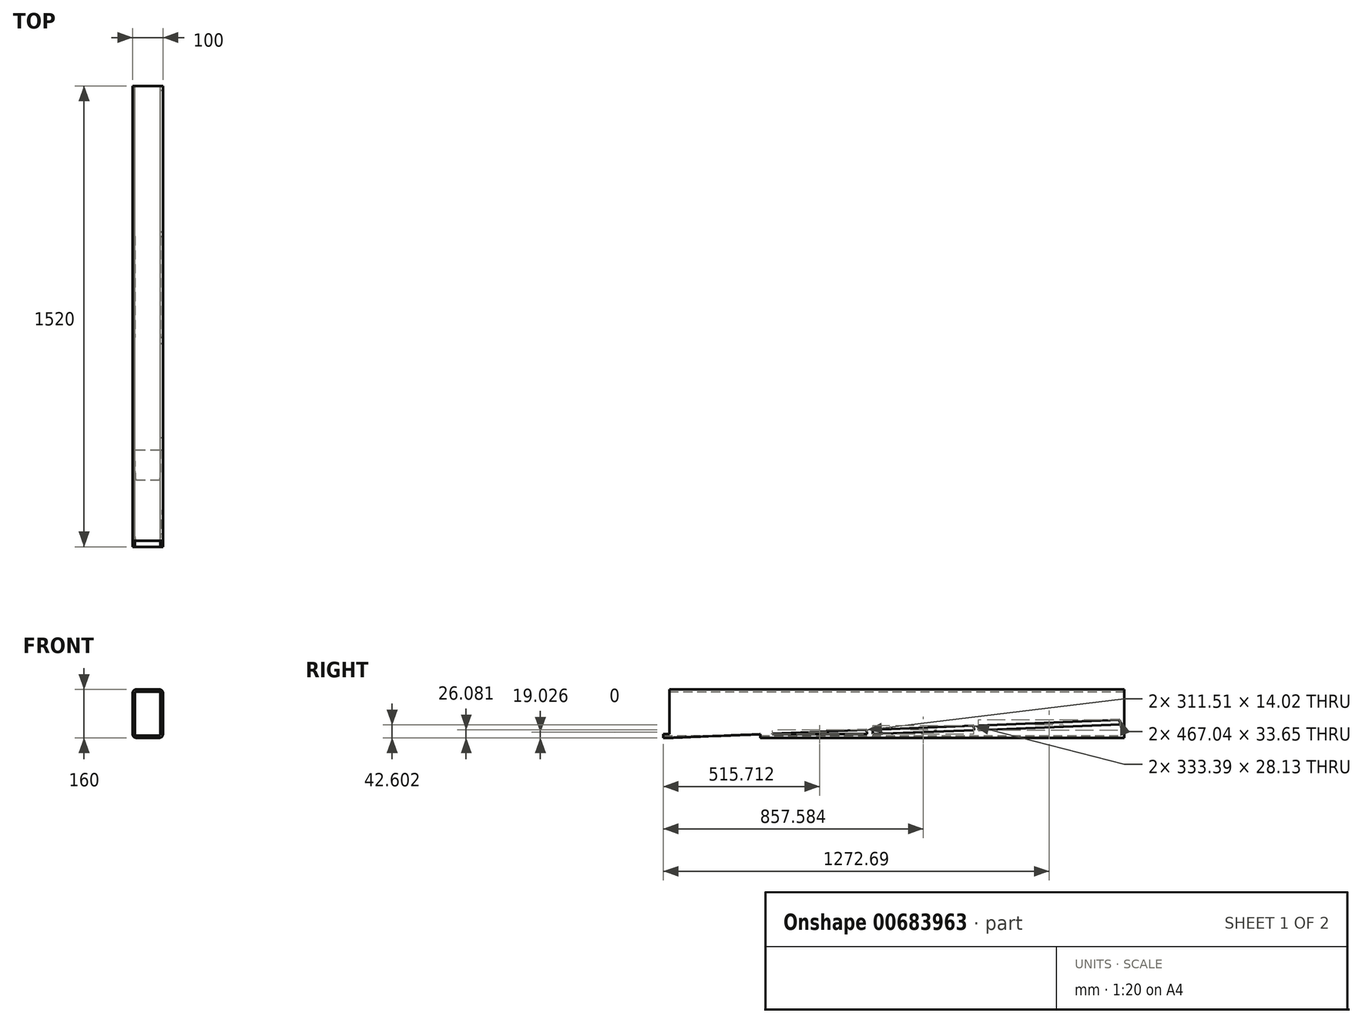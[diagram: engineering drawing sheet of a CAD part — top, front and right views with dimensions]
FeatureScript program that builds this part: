
annotation { "Feature Type Name" : "Feature", "Feature Type Description" : "" }
export const myFeature = defineFeature(function(context is Context, id is Id, definition is map)
    precondition{}
    {
        {
            var Q0;
            Q0=qCreatedBy(makeId("Front.planeOp"),FACE);
            var sketch = newSketch(context, id + "F0", { "sketchPlane" : qUnion([Q0])});
            skLineSegment(sketch, "E0.bottom", {"start": v(-38, 80) * mm, "end": v(38, 80) * mm});
            skLineSegment(sketch, "E0.top", {"start": v(-38, -80) * mm, "end": v(38, -80) * mm});
            skLineSegment(sketch, "E0.left", {"start": v(-50, 68) * mm, "end": v(-50, -68) * mm});
            skLineSegment(sketch, "E0.right", {"start": v(50, 68) * mm, "end": v(50, -68) * mm});
            skPoint(sketch, "E1", {"position": v(0, 80) * mm});
            skPoint(sketch, "E2", {"position": v(50, 0) * mm});
            skPoint(sketch, "E3.visualSharp", {"position": v(-50, 80) * mm});
            skArc(sketch, "E3.filletArc", {"start": v(-38, 80) * mm, "mid": v(-46.49, 76.49) * mm, "end": v(-50, 68) * mm});
            skPoint(sketch, "E4.visualSharp", {"position": v(50, 80) * mm});
            skArc(sketch, "E4.filletArc", {"start": v(50, 68) * mm, "mid": v(46.49, 76.49) * mm, "end": v(38, 80) * mm});
            skPoint(sketch, "E5.visualSharp", {"position": v(50, -80) * mm});
            skArc(sketch, "E5.filletArc", {"start": v(38, -80) * mm, "mid": v(46.49, -76.49) * mm, "end": v(50, -68) * mm});
            skPoint(sketch, "E6.visualSharp", {"position": v(-50, -80) * mm});
            skArc(sketch, "E6.filletArc", {"start": v(-50, -68) * mm, "mid": v(-46.49, -76.49) * mm, "end": v(-38, -80) * mm});
            skArc(sketch, "E7.0", {"start": v(42, 68) * mm, "mid": v(40.83, 70.83) * mm, "end": v(38, 72) * mm});
            skLineSegment(sketch, "E7.1", {"start": v(-38, 72) * mm, "end": v(38, 72) * mm});
            skLineSegment(sketch, "E7.2", {"start": v(42, 68) * mm, "end": v(42, -68) * mm});
            skArc(sketch, "E7.3", {"start": v(-38, 72) * mm, "mid": v(-40.83, 70.83) * mm, "end": v(-42, 68) * mm});
            skArc(sketch, "E7.4", {"start": v(38, -72) * mm, "mid": v(40.83, -70.83) * mm, "end": v(42, -68) * mm});
            skLineSegment(sketch, "E7.5", {"start": v(-38, -72) * mm, "end": v(38, -72) * mm});
            skArc(sketch, "E7.6", {"start": v(-42, -68) * mm, "mid": v(-40.83, -70.83) * mm, "end": v(-38, -72) * mm});
            skLineSegment(sketch, "E7.7", {"start": v(-42, 68) * mm, "end": v(-42, -68) * mm});
            skSolve(sketch);
        }
        {
            var Q0;
            Q0=makeQuery(id+"F0.imprint","IMPRINT",FACE,{"disambiguationData":[TD([[makeQuery(id+"F0.imprint","IMPRINT",EDGE,{"derivedFrom":sQuery(id+"F0.wireOp",EDGE,"E0.bottom")}),-1.0]])]});
            extrude(context, id + "F1", {"entities" : qUnion([Q0]), "depth" : 1520 * mm, "offsetDistance" : 25.4 * mm});
        }
        {
            var Q0;
            Q0=qCreatedBy(makeId("Right.planeOp"),FACE);
            var sketch = newSketch(context, id + "F2", { "sketchPlane" : qUnion([Q0])});
            skPoint(sketch, "E8", {"position": v(-1500, -80) * mm});
            skLineSegment(sketch, "E9", {"start": v(-1500, -80) * mm, "end": v(-1200, -68) * mm});
            skLineSegment(sketch, "E10", {"start": v(0, -20) * mm, "end": v(0, -80) * mm});
            skLineSegment(sketch, "E11", {"start": v(0, -80) * mm, "end": v(-1500, -80) * mm});
            skLineSegment(sketch, "E12", {"start": v(-1200, -68) * mm, "end": v(-1199.53, -80) * mm});
            skLineSegment(sketch, "E13", {"start": v(-1199.53, -80) * mm, "end": v(-1159.5, -80) * mm});
            skLineSegment(sketch, "E14", {"start": v(-1159.5, -80) * mm, "end": v(-1160.04, -66.4) * mm});
            skLineSegment(sketch, "E15.trimOffspring", {"start": v(-1160.04, -66.4) * mm, "end": v(0, -20) * mm, "construction": true});
            skLineSegment(sketch, "E16", {"start": v(-1160.04, -66.4) * mm, "end": v(-1160.04, -67.98) * mm});
            skLineSegment(sketch, "E17", {"start": v(-1160.04, -67.98) * mm, "end": v(-486, -67.98) * mm});
            skLineSegment(sketch, "E18", {"start": v(-480.83, -39.23) * mm, "end": v(-480.23, -54.22) * mm});
            skLineSegment(sketch, "E19", {"start": v(-480.23, -54.22) * mm, "end": v(-13.79, -35.56) * mm});
            skLineSegment(sketch, "E20", {"start": v(-13.79, -35.56) * mm, "end": v(-14.39, -20.58) * mm});
            skLineSegment(sketch, "E21", {"start": v(-496.31, -39.85) * mm, "end": v(-495.72, -54.67) * mm});
            skLineSegment(sketch, "E22", {"start": v(-495.72, -54.67) * mm, "end": v(-828.52, -67.98) * mm});
            skLineSegment(sketch, "E23", {"start": v(-828.52, -67.98) * mm, "end": v(-829.11, -53.16) * mm});
            skLineSegment(sketch, "E24", {"start": v(-829.11, -53.16) * mm, "end": v(-496.31, -39.85) * mm});
            skLineSegment(sketch, "E25", {"start": v(-849.1, -53.96) * mm, "end": v(-848.53, -67.98) * mm});
            skLineSegment(sketch, "E26", {"start": v(-848.53, -67.98) * mm, "end": v(-1160.04, -67.98) * mm});
            skLineSegment(sketch, "E27", {"start": v(-1160.04, -66.4) * mm, "end": v(-849.1, -53.96) * mm});
            skLineSegment(sketch, "E28", {"start": v(-480.83, -39.23) * mm, "end": v(-14.39, -20.58) * mm});
            skLineSegment(sketch, "E29.bottom", {"start": v(-1524.83, 85.4) * mm, "end": v(-1500, 85.4) * mm});
            skLineSegment(sketch, "E29.top", {"start": v(-1524.83, -67.76) * mm, "end": v(-1500, -67.76) * mm});
            skLineSegment(sketch, "E29.left", {"start": v(-1524.83, 85.4) * mm, "end": v(-1524.83, -67.76) * mm});
            skLineSegment(sketch, "E29.right", {"start": v(-1500, 85.4) * mm, "end": v(-1500, -67.76) * mm});
            skSolve(sketch);
        }
        {
            var Q0;
            Q0 = qSketchRegion(id + "F2", true);
            extrude(context, id + "F3", {"entities" : qUnion([Q0]), "operationType" : NewBodyOperationType.REMOVE, "endBound" : BoundingType.THROUGH_ALL, "oppositeDirection" : true, "depth" : 25.4 * mm, "offsetDistance" : 25.4 * mm, "hasSecondDirection" : true, "secondDirectionBound" : SecondDirectionBoundingType.THROUGH_ALL, "secondDirectionOppositeDirection" : false, "secondDirectionDepth" : 25.4 * mm});
        }
    });
